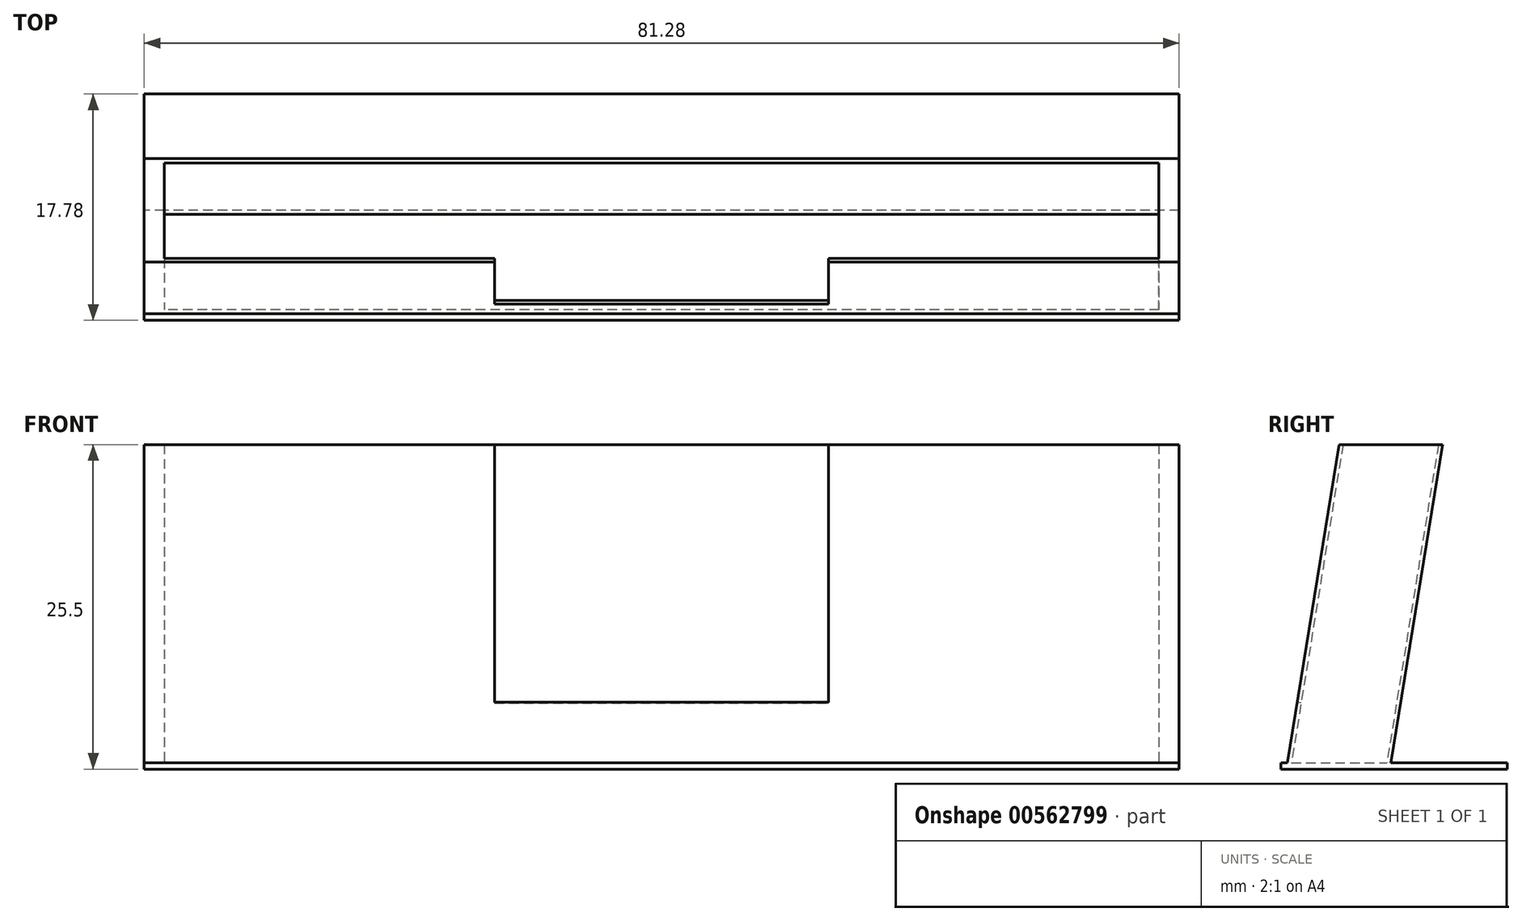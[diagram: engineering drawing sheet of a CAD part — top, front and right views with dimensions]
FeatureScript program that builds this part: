
annotation { "Feature Type Name" : "Feature", "Feature Type Description" : "" }
export const myFeature = defineFeature(function(context is Context, id is Id, definition is map)
    precondition{}
    {
        {
            var Q0;
            Q0=qCreatedBy(makeId("Top.planeOp"),FACE);
            cPlane(context, id + "F0", {"entities" : qUnion([Q0]), "cplaneType" : CPlaneType.OFFSET, "offset" : 25 * mm, "width" : 152.4 * mm, "height" : 152.4 * mm});
        }
        {
            var Q0;
            Q0=qCreatedBy(makeId("Top.planeOp"),FACE);
            var sketch = newSketch(context, id + "F1", { "sketchPlane" : qUnion([Q0])});
            skLineSegment(sketch, "E0.bottom", {"start": v(40.64, -4.06) * mm, "end": v(-40.64, -4.06) * mm});
            skLineSegment(sketch, "E0.top", {"start": v(40.64, 4.06) * mm, "end": v(-40.64, 4.06) * mm});
            skLineSegment(sketch, "E0.left", {"start": v(40.64, -4.06) * mm, "end": v(40.64, 4.06) * mm});
            skLineSegment(sketch, "E0.right", {"start": v(-40.64, -4.06) * mm, "end": v(-40.64, 4.06) * mm});
            skPoint(sketch, "E0.middle", {"position": v(0, 0) * mm});
            skSolve(sketch);
        }
        {
            var Q0;
            Q0=qCreatedBy(id+"F0.planeOp",FACE);
            var sketch = newSketch(context, id + "F2", { "sketchPlane" : qUnion([Q0])});
            skLineSegment(sketch, "E1.bottom", {"start": v(-40.64, 0) * mm, "end": v(40.64, 0) * mm});
            skLineSegment(sketch, "E1.top", {"start": v(-40.64, 8.13) * mm, "end": v(40.64, 8.13) * mm});
            skLineSegment(sketch, "E1.left", {"start": v(-40.64, 0) * mm, "end": v(-40.64, 8.13) * mm});
            skLineSegment(sketch, "E1.right", {"start": v(40.64, 0) * mm, "end": v(40.64, 8.13) * mm});
            skPoint(sketch, "E1.middle", {"position": v(0, 4.06) * mm});
            skSolve(sketch);
        }
        {
            var Q0;
            Q0 = qSketchRegion(id + "F1", true);
            var Q1;
            Q1 = qSketchRegion(id + "F2", true);
            loft(context, id + "F3", {"sheetProfilesArray" : [{ "sheetProfileEntities" : qUnion([Q0]) }, { "sheetProfileEntities" : qUnion([Q1]) }]});
        }
        {
            var Q0;
            Q0=makeQuery(id+"F3.opLoft","SWEPT_FACE",FACE,{"disambiguationData":[OSD([sQuery(id+"F1.wireOp",EDGE,"E0.bottom"),sQuery(id+"F1.wireOp",EDGE,"E0.left"),sQuery(id+"F1.wireOp",EDGE,"E0.right"),sQuery(id+"F2.wireOp",EDGE,"E1.bottom"),sQuery(id+"F2.wireOp",EDGE,"E1.left"),sQuery(id+"F2.wireOp",EDGE,"E1.right")])]});
            var sketch = newSketch(context, id + "F4", { "sketchPlane" : qUnion([Q0])});
            skPoint(sketch, "E2.middle", {"position": v(0, 0) * mm});
            skLineSegment(sketch, "E3.bottom", {"start": v(13.12, 4.16) * mm, "end": v(-13.12, 4.16) * mm});
            skLineSegment(sketch, "E3.left", {"start": v(13.12, 4.16) * mm, "end": v(13.12, 24.72) * mm});
            skLineSegment(sketch, "E3.right", {"start": v(-13.12, 4.16) * mm, "end": v(-13.12, 24.72) * mm});
            skPoint(sketch, "E3.middle", {"position": v(0, 24.68) * mm});
            skLineSegment(sketch, "E4", {"start": v(-13.12, 24.72) * mm, "end": v(13.12, 24.72) * mm});
            skSolve(sketch);
        }
        {
            var Q0;
            Q0 = qSketchRegion(id + "F4", true);
            extrude(context, id + "F5", {"entities" : qUnion([Q0]), "operationType" : NewBodyOperationType.REMOVE, "oppositeDirection" : true, "depth" : 1 * mm, "offsetDistance" : 25.4 * mm});
        }
        {
            var Q0;
            Q0=qCreatedBy(id+"F0.planeOp",FACE);
            var sketch = newSketch(context, id + "F6", { "sketchPlane" : qUnion([Q0])});
            skLineSegment(sketch, "E5.bottom", {"start": v(39.05, 0.3) * mm, "end": v(-39.05, 0.3) * mm});
            skLineSegment(sketch, "E5.top", {"start": v(39.05, 7.8) * mm, "end": v(-39.05, 7.8) * mm});
            skLineSegment(sketch, "E5.left", {"start": v(39.05, 0.3) * mm, "end": v(39.05, 7.8) * mm});
            skLineSegment(sketch, "E5.right", {"start": v(-39.05, 0.3) * mm, "end": v(-39.05, 7.8) * mm});
            skPoint(sketch, "E5.middle", {"position": v(0, 4.04) * mm});
            skSolve(sketch);
        }
        {
            var Q0;
            Q0=qCreatedBy(makeId("Top.planeOp"),FACE);
            var sketch = newSketch(context, id + "F7", { "sketchPlane" : qUnion([Q0])});
            skLineSegment(sketch, "E6.bottom", {"start": v(39.05, -3.75) * mm, "end": v(-39.05, -3.75) * mm});
            skLineSegment(sketch, "E6.top", {"start": v(39.05, 3.75) * mm, "end": v(-39.05, 3.75) * mm});
            skLineSegment(sketch, "E6.left", {"start": v(39.05, -3.75) * mm, "end": v(39.05, 3.75) * mm});
            skLineSegment(sketch, "E6.right", {"start": v(-39.05, -3.75) * mm, "end": v(-39.05, 3.75) * mm});
            skPoint(sketch, "E6.middle", {"position": v(0, 0) * mm});
            skSolve(sketch);
        }
        {
            var Q1;
            Q1 = qSketchRegion(id + "F6", true);
            var Q2;
            Q2 = qSketchRegion(id + "F7", true);
            loft(context, id + "F8", {"operationType" : NewBodyOperationType.REMOVE, "sheetProfilesArray" : [{ "sheetProfileEntities" : qUnion([Q1]) }, { "sheetProfileEntities" : qUnion([Q2]) }]});
        }
        {
            var Q0;
            Q0=qCreatedBy(makeId("Top.planeOp"),FACE);
            var sketch = newSketch(context, id + "F9", { "sketchPlane" : qUnion([Q0])});
            skLineSegment(sketch, "E7.bottom", {"start": v(40.64, 13.2) * mm, "end": v(-40.64, 13.2) * mm});
            skLineSegment(sketch, "E7.top", {"start": v(40.64, -4.57) * mm, "end": v(-40.64, -4.57) * mm});
            skLineSegment(sketch, "E7.left", {"start": v(40.64, 13.2) * mm, "end": v(40.64, -4.57) * mm});
            skLineSegment(sketch, "E7.right", {"start": v(-40.64, 13.2) * mm, "end": v(-40.64, -4.57) * mm});
            skPoint(sketch, "E7.middle", {"position": v(0, 4.32) * mm});
            skSolve(sketch);
        }
        {
            var Q0;
            Q0 = qSketchRegion(id + "F9", true);
            extrude(context, id + "F10", {"entities" : qUnion([Q0]), "operationType" : NewBodyOperationType.ADD, "oppositeDirection" : true, "depth" : 0.5 * mm, "offsetDistance" : 25.4 * mm});
        }
    });
